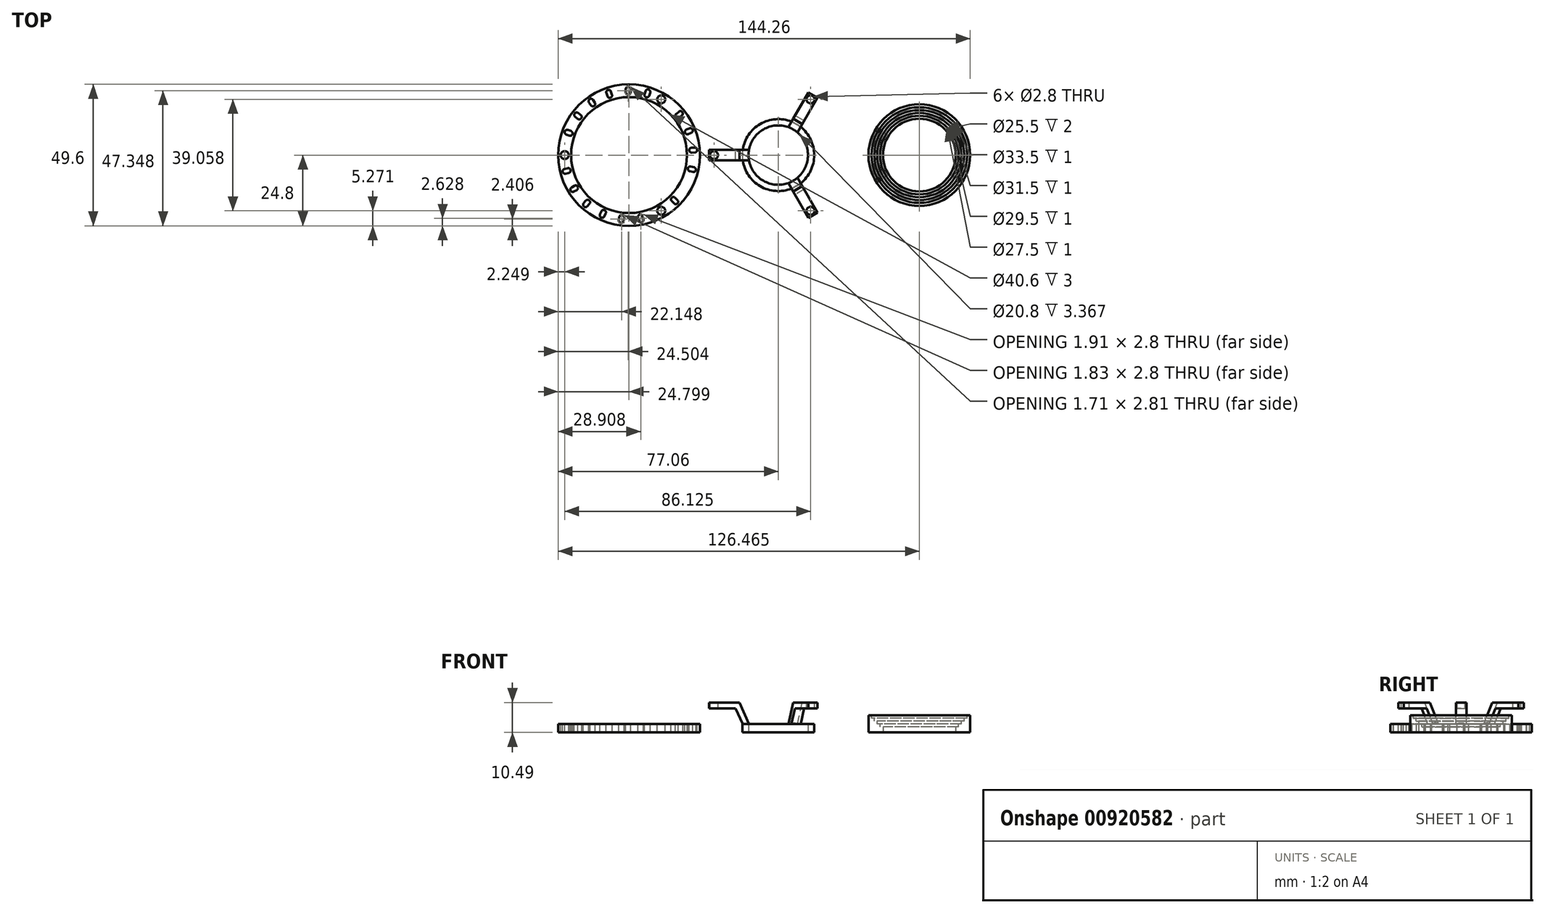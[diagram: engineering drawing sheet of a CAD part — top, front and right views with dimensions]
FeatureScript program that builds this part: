
annotation { "Feature Type Name" : "Feature", "Feature Type Description" : "" }
export const myFeature = defineFeature(function(context is Context, id is Id, definition is map)
    precondition{}
    {
        {
            var Q0;
            Q0=qCreatedBy(makeId("Top.planeOp"),FACE);
            var sketch = newSketch(context, id + "F0", { "sketchPlane" : qUnion([Q0])});
            skCircle(sketch, "E0", {"center": v(-52.66, 0) * mm, "radius": 24.8 * mm});
            skCircle(sketch, "E1", {"center": v(-52.66, 0) * mm, "radius": 20.3 * mm});
            skCircle(sketch, "E2.0", {"center": v(49, 0) * mm, "radius": 17.8 * mm});
            skCircle(sketch, "E3.0", {"center": v(49, 0) * mm, "radius": 12.75 * mm});
            skCircle(sketch, "E4.0", {"center": v(0, 0) * mm, "radius": 12.6 * mm});
            skCircle(sketch, "E5.0", {"center": v(0, 0) * mm, "radius": 10.4 * mm});
            skSolve(sketch);
        }
        {
            var Q0;
            Q0=makeQuery(id+"F0.imprint","IMPRINT",FACE,{"disambiguationData":[TD([[makeQuery(id+"F0.imprint","IMPRINT",EDGE,{"derivedFrom":sQuery(id+"F0.wireOp",EDGE,"E0")}),1.0]])]});
            var Q1;
            Q1=makeQuery(id+"F0.imprint","IMPRINT",FACE,{"disambiguationData":[TD([[makeQuery(id+"F0.imprint","IMPRINT",EDGE,{"derivedFrom":sQuery(id+"F0.wireOp",EDGE,"E4.0")}),1.0]])]});
            extrude(context, id + "F1", {"entities" : qUnion([Q0, Q1]), "depth" : 3 * mm, "offsetDistance" : 25 * mm});
        }
        {
            var Q0;
            Q0=makeQuery(id+"F1.opExtrude","CAP_FACE",FACE,{"disambiguationData":[OSD([sQuery(id+"F0.wireOp",EDGE,"E0"),sQuery(id+"F0.wireOp",EDGE,"E1")])],"isStart":false});
            var sketch = newSketch(context, id + "F2", { "sketchPlane" : qUnion([Q0])});
            skLineSegment(sketch, "E6", {"start": v(-72.96, 0) * mm, "end": v(-77.46, 0) * mm, "construction": true});
            skLineSegment(sketch, "E7.bottom", {"start": v(-72.88, 1.83) * mm, "end": v(-77.54, 1.83) * mm, "construction": true});
            skLineSegment(sketch, "E7.top", {"start": v(-72.88, -1.83) * mm, "end": v(-77.54, -1.83) * mm, "construction": true});
            skLineSegment(sketch, "E7.left", {"start": v(-72.88, 1.83) * mm, "end": v(-72.88, -1.83) * mm, "construction": true});
            skLineSegment(sketch, "E7.right", {"start": v(-77.54, 1.83) * mm, "end": v(-77.54, -1.83) * mm, "construction": true});
            skPoint(sketch, "E7.middle", {"position": v(-75.21, 0) * mm});
            skCircle(sketch, "E8", {"center": v(-75.21, 0) * mm, "radius": 1.4 * mm});
            skLineSegment(sketch, "E9.1.0", {"start": v(-40.72, 17.03) * mm, "end": v(-38.89, 20.2) * mm, "construction": true});
            skLineSegment(sketch, "E9.1.1", {"start": v(-43.89, 18.86) * mm, "end": v(-42.06, 22.03) * mm, "construction": true});
            skCircle(sketch, "E9.1.2", {"center": v(-41.39, 19.53) * mm, "radius": 1.4 * mm});
            skPoint(sketch, "E9.1.3", {"position": v(-41.39, 19.53) * mm});
            skLineSegment(sketch, "E9.1.4", {"start": v(-42.26, 18.01) * mm, "end": v(-40.51, 21.04) * mm, "construction": true});
            skLineSegment(sketch, "E9.1.5", {"start": v(-38.89, 20.2) * mm, "end": v(-42.06, 22.03) * mm, "construction": true});
            skLineSegment(sketch, "E9.1.6", {"start": v(-40.72, 17.03) * mm, "end": v(-43.89, 18.86) * mm, "construction": true});
            skLineSegment(sketch, "E9.2.0", {"start": v(-43.89, -18.86) * mm, "end": v(-42.06, -22.03) * mm, "construction": true});
            skLineSegment(sketch, "E9.2.1", {"start": v(-40.72, -17.03) * mm, "end": v(-38.89, -20.2) * mm, "construction": true});
            skCircle(sketch, "E9.2.2", {"center": v(-41.39, -19.53) * mm, "radius": 1.4 * mm});
            skPoint(sketch, "E9.2.3", {"position": v(-41.39, -19.53) * mm});
            skLineSegment(sketch, "E9.2.4", {"start": v(-42.26, -18.01) * mm, "end": v(-40.51, -21.04) * mm, "construction": true});
            skLineSegment(sketch, "E9.2.5", {"start": v(-42.06, -22.03) * mm, "end": v(-38.89, -20.2) * mm, "construction": true});
            skLineSegment(sketch, "E9.2.6", {"start": v(-43.89, -18.86) * mm, "end": v(-40.72, -17.03) * mm, "construction": true});
            skPoint(sketch, "E9.center", {"position": v(-52.66, 0) * mm});
            skLineSegment(sketch, "E10", {"start": v(-32.36, 0) * mm, "end": v(-27.86, 0) * mm, "construction": true});
            skLineSegment(sketch, "E11.left", {"start": v(-28.7, 0.05) * mm, "end": v(-28.7, -0.05) * mm});
            skLineSegment(sketch, "E11.right", {"start": v(-31.51, 0.05) * mm, "end": v(-31.51, -0.05) * mm});
            skPoint(sketch, "E11.middle", {"position": v(-30.11, 0) * mm});
            skPoint(sketch, "E12.visualSharp", {"position": v(-28.7, 0.85) * mm});
            skPoint(sketch, "E13.visualSharp", {"position": v(-31.51, 0.85) * mm});
            skPoint(sketch, "E14.visualSharp", {"position": v(-31.51, -0.85) * mm});
            skPoint(sketch, "E15.visualSharp", {"position": v(-28.7, -0.85) * mm});
            skPoint(sketch, "E16.1.0", {"position": v(-29.74, -7.02) * mm});
            skPoint(sketch, "E16.1.1", {"position": v(-32.45, -6.3) * mm});
            skPoint(sketch, "E16.1.2", {"position": v(-32.01, -4.66) * mm});
            skPoint(sketch, "E16.1.3", {"position": v(-29.3, -5.38) * mm});
            skPoint(sketch, "E16.1.4", {"position": v(-30.88, -5.84) * mm});
            skLineSegment(sketch, "E16.1.11", {"start": v(-32.57, -5.38) * mm, "end": v(-29.19, -6.29) * mm, "construction": true});
            skLineSegment(sketch, "E16.1.12", {"start": v(-32.22, -5.43) * mm, "end": v(-32.25, -5.52) * mm});
            skLineSegment(sketch, "E16.1.13", {"start": v(-29.51, -6.16) * mm, "end": v(-29.54, -6.24) * mm});
            skPoint(sketch, "E16.2.0", {"position": v(-32.34, -12.7) * mm});
            skPoint(sketch, "E16.2.1", {"position": v(-34.77, -11.3) * mm});
            skPoint(sketch, "E16.2.2", {"position": v(-33.92, -9.84) * mm});
            skPoint(sketch, "E16.2.3", {"position": v(-31.5, -11.24) * mm});
            skPoint(sketch, "E16.2.4", {"position": v(-33.13, -11.27) * mm});
            skLineSegment(sketch, "E16.2.11", {"start": v(-34.65, -10.4) * mm, "end": v(-31.62, -12.15) * mm, "construction": true});
            skLineSegment(sketch, "E16.2.12", {"start": v(-34.32, -10.53) * mm, "end": v(-34.37, -10.61) * mm});
            skLineSegment(sketch, "E16.2.13", {"start": v(-31.9, -11.94) * mm, "end": v(-31.94, -12.02) * mm});
            skPoint(sketch, "E16.3.0", {"position": v(-36.32, -17.53) * mm});
            skPoint(sketch, "E16.3.1", {"position": v(-38.3, -15.55) * mm});
            skPoint(sketch, "E16.3.2", {"position": v(-37.1, -14.36) * mm});
            skPoint(sketch, "E16.3.3", {"position": v(-35.13, -16.34) * mm});
            skPoint(sketch, "E16.3.4", {"position": v(-36.72, -15.95) * mm});
            skArc(sketch, "E16.3.5", {"start": v(-37.74, -14.99) * mm, "mid": v(-37.97, -15.55) * mm, "end": v(-37.74, -16.12) * mm});
            skArc(sketch, "E16.3.6", {"start": v(-36.89, -16.97) * mm, "mid": v(-36.32, -17.2) * mm, "end": v(-35.76, -16.97) * mm});
            skArc(sketch, "E16.3.7", {"start": v(-36.54, -14.92) * mm, "mid": v(-37.1, -14.69) * mm, "end": v(-37.68, -14.92) * mm});
            skArc(sketch, "E16.3.8", {"start": v(-35.7, -16.9) * mm, "mid": v(-35.46, -16.34) * mm, "end": v(-35.7, -15.77) * mm});
            skLineSegment(sketch, "E16.3.9", {"start": v(-35.7, -15.77) * mm, "end": v(-36.54, -14.92) * mm});
            skLineSegment(sketch, "E16.3.10", {"start": v(-36.89, -16.97) * mm, "end": v(-37.74, -16.12) * mm});
            skLineSegment(sketch, "E16.3.11", {"start": v(-37.95, -14.7) * mm, "end": v(-35.48, -17.18) * mm, "construction": true});
            skLineSegment(sketch, "E16.3.12", {"start": v(-37.68, -14.92) * mm, "end": v(-37.74, -14.99) * mm});
            skLineSegment(sketch, "E16.3.13", {"start": v(-35.7, -16.9) * mm, "end": v(-35.76, -16.97) * mm});
            skLineSegment(sketch, "E17.1.0", {"start": v(-42.77, -18.7) * mm, "end": v(-42.85, -18.74) * mm});
            skLineSegment(sketch, "E17.1.1", {"start": v(-41.47, -21.18) * mm, "end": v(-41.55, -21.22) * mm});
            skPoint(sketch, "E17.1.2", {"position": v(-42.26, -21.6) * mm});
            skArc(sketch, "E17.1.3", {"start": v(-41.7, -19.03) * mm, "mid": v(-42.16, -18.64) * mm, "end": v(-42.77, -18.7) * mm});
            skArc(sketch, "E17.1.4", {"start": v(-42.63, -20.88) * mm, "mid": v(-42.16, -21.27) * mm, "end": v(-41.55, -21.22) * mm});
            skArc(sketch, "E17.1.5", {"start": v(-42.85, -18.74) * mm, "mid": v(-43.25, -19.2) * mm, "end": v(-43.2, -19.82) * mm});
            skLineSegment(sketch, "E17.1.6", {"start": v(-42.98, -18.4) * mm, "end": v(-41.35, -21.5) * mm, "construction": true});
            skPoint(sketch, "E17.1.7", {"position": v(-42.16, -19.96) * mm});
            skPoint(sketch, "E17.1.8", {"position": v(-42.07, -18.32) * mm});
            skLineSegment(sketch, "E17.1.9", {"start": v(-41.13, -20.1) * mm, "end": v(-41.7, -19.03) * mm});
            skLineSegment(sketch, "E17.1.10", {"start": v(-42.63, -20.88) * mm, "end": v(-43.2, -19.82) * mm});
            skPoint(sketch, "E17.1.11", {"position": v(-40.76, -20.8) * mm});
            skPoint(sketch, "E17.1.12", {"position": v(-43.56, -19.1) * mm});
            skArc(sketch, "E17.1.13", {"start": v(-41.47, -21.18) * mm, "mid": v(-41.08, -20.7) * mm, "end": v(-41.13, -20.1) * mm});
            skLineSegment(sketch, "E17.2.0", {"start": v(-48.76, -20.79) * mm, "end": v(-48.85, -20.8) * mm});
            skLineSegment(sketch, "E17.2.1", {"start": v(-48.25, -23.54) * mm, "end": v(-48.34, -23.56) * mm});
            skPoint(sketch, "E17.2.2", {"position": v(-49.13, -23.7) * mm});
            skArc(sketch, "E17.2.3", {"start": v(-47.83, -21.43) * mm, "mid": v(-48.16, -20.91) * mm, "end": v(-48.76, -20.79) * mm});
            skArc(sketch, "E17.2.4", {"start": v(-49.27, -22.92) * mm, "mid": v(-48.94, -23.43) * mm, "end": v(-48.34, -23.56) * mm});
            skArc(sketch, "E17.2.5", {"start": v(-48.85, -20.8) * mm, "mid": v(-49.37, -21.14) * mm, "end": v(-49.5, -21.73) * mm});
            skLineSegment(sketch, "E17.2.6", {"start": v(-48.87, -20.45) * mm, "end": v(-48.23, -23.9) * mm, "construction": true});
            skPoint(sketch, "E17.2.7", {"position": v(-48.55, -22.17) * mm});
            skPoint(sketch, "E17.2.8", {"position": v(-47.98, -20.64) * mm});
            skLineSegment(sketch, "E17.2.9", {"start": v(-47.61, -22.6) * mm, "end": v(-47.83, -21.43) * mm});
            skLineSegment(sketch, "E17.2.10", {"start": v(-49.27, -22.92) * mm, "end": v(-49.5, -21.73) * mm});
            skPoint(sketch, "E17.2.11", {"position": v(-47.46, -23.4) * mm});
            skPoint(sketch, "E17.2.12", {"position": v(-49.64, -20.95) * mm});
            skArc(sketch, "E17.2.13", {"start": v(-48.25, -23.54) * mm, "mid": v(-47.74, -23.2) * mm, "end": v(-47.61, -22.6) * mm});
            skLineSegment(sketch, "E17.3.0", {"start": v(-55.1, -21) * mm, "end": v(-55.2, -21) * mm});
            skLineSegment(sketch, "E17.3.1", {"start": v(-55.43, -23.8) * mm, "end": v(-55.52, -23.78) * mm});
            skPoint(sketch, "E17.3.2", {"position": v(-56.32, -23.69) * mm});
            skArc(sketch, "E17.3.3", {"start": v(-54.4, -21.9) * mm, "mid": v(-54.57, -21.3) * mm, "end": v(-55.1, -21) * mm});
            skArc(sketch, "E17.3.4", {"start": v(-56.22, -22.9) * mm, "mid": v(-56.06, -23.48) * mm, "end": v(-55.52, -23.78) * mm});
            skArc(sketch, "E17.3.5", {"start": v(-55.2, -21) * mm, "mid": v(-55.78, -21.16) * mm, "end": v(-56.08, -21.7) * mm});
            skLineSegment(sketch, "E17.3.6", {"start": v(-55.1, -20.66) * mm, "end": v(-55.52, -24.13) * mm, "construction": true});
            skPoint(sketch, "E17.3.7", {"position": v(-55.31, -22.4) * mm});
            skPoint(sketch, "E17.3.8", {"position": v(-54.3, -21.1) * mm});
            skLineSegment(sketch, "E17.3.9", {"start": v(-54.54, -23.1) * mm, "end": v(-54.4, -21.9) * mm});
            skLineSegment(sketch, "E17.3.10", {"start": v(-56.22, -22.9) * mm, "end": v(-56.08, -21.7) * mm});
            skPoint(sketch, "E17.3.11", {"position": v(-54.64, -23.89) * mm});
            skPoint(sketch, "E17.3.12", {"position": v(-55.99, -20.9) * mm});
            skArc(sketch, "E17.3.13", {"start": v(-55.43, -23.8) * mm, "mid": v(-54.84, -23.63) * mm, "end": v(-54.54, -23.1) * mm});
            skLineSegment(sketch, "E17.4.0", {"start": v(-61.22, -19.34) * mm, "end": v(-61.3, -19.3) * mm});
            skLineSegment(sketch, "E17.4.1", {"start": v(-62.36, -21.9) * mm, "end": v(-62.44, -21.86) * mm});
            skPoint(sketch, "E17.4.2", {"position": v(-63.18, -21.54) * mm});
            skArc(sketch, "E17.4.3", {"start": v(-60.82, -20.4) * mm, "mid": v(-60.8, -19.78) * mm, "end": v(-61.22, -19.34) * mm});
            skArc(sketch, "E17.4.4", {"start": v(-62.85, -20.8) * mm, "mid": v(-62.87, -21.42) * mm, "end": v(-62.44, -21.86) * mm});
            skArc(sketch, "E17.4.5", {"start": v(-61.3, -19.3) * mm, "mid": v(-61.92, -19.29) * mm, "end": v(-62.36, -19.7) * mm});
            skLineSegment(sketch, "E17.4.6", {"start": v(-61.12, -19) * mm, "end": v(-62.54, -22.2) * mm, "construction": true});
            skPoint(sketch, "E17.4.7", {"position": v(-61.83, -20.6) * mm});
            skPoint(sketch, "E17.4.8", {"position": v(-60.49, -19.66) * mm});
            skLineSegment(sketch, "E17.4.9", {"start": v(-61.3, -21.5) * mm, "end": v(-60.82, -20.4) * mm});
            skLineSegment(sketch, "E17.4.10", {"start": v(-62.85, -20.8) * mm, "end": v(-62.36, -19.7) * mm});
            skPoint(sketch, "E17.4.11", {"position": v(-61.63, -22.23) * mm});
            skPoint(sketch, "E17.4.12", {"position": v(-62.04, -18.98) * mm});
            skArc(sketch, "E17.4.13", {"start": v(-62.36, -21.9) * mm, "mid": v(-61.75, -21.92) * mm, "end": v(-61.3, -21.5) * mm});
            skLineSegment(sketch, "E17.5.0", {"start": v(-66.57, -15.93) * mm, "end": v(-66.64, -15.87) * mm});
            skLineSegment(sketch, "E17.5.1", {"start": v(-68.42, -18.04) * mm, "end": v(-68.49, -17.98) * mm});
            skPoint(sketch, "E17.5.2", {"position": v(-69.09, -17.45) * mm});
            skArc(sketch, "E17.5.3", {"start": v(-66.5, -17.06) * mm, "mid": v(-66.3, -16.48) * mm, "end": v(-66.57, -15.93) * mm});
            skArc(sketch, "E17.5.4", {"start": v(-68.56, -16.85) * mm, "mid": v(-68.76, -17.43) * mm, "end": v(-68.49, -17.98) * mm});
            skArc(sketch, "E17.5.5", {"start": v(-66.64, -15.87) * mm, "mid": v(-67.22, -15.67) * mm, "end": v(-67.77, -15.94) * mm});
            skLineSegment(sketch, "E17.5.6", {"start": v(-66.38, -15.64) * mm, "end": v(-68.68, -18.27) * mm, "construction": true});
            skPoint(sketch, "E17.5.7", {"position": v(-67.53, -16.95) * mm});
            skPoint(sketch, "E17.5.8", {"position": v(-65.97, -16.46) * mm});
            skLineSegment(sketch, "E17.5.9", {"start": v(-67.3, -17.96) * mm, "end": v(-66.5, -17.06) * mm});
            skLineSegment(sketch, "E17.5.10", {"start": v(-68.56, -16.85) * mm, "end": v(-67.77, -15.94) * mm});
            skPoint(sketch, "E17.5.11", {"position": v(-67.82, -18.57) * mm});
            skPoint(sketch, "E17.5.12", {"position": v(-67.24, -15.34) * mm});
            skArc(sketch, "E17.5.13", {"start": v(-68.42, -18.04) * mm, "mid": v(-67.84, -18.24) * mm, "end": v(-67.3, -17.96) * mm});
            skLineSegment(sketch, "E17.6.0", {"start": v(-70.67, -11.09) * mm, "end": v(-70.72, -11.01) * mm});
            skLineSegment(sketch, "E17.6.1", {"start": v(-73.06, -12.55) * mm, "end": v(-73.1, -12.48) * mm});
            skPoint(sketch, "E17.6.2", {"position": v(-73.53, -11.8) * mm});
            skArc(sketch, "E17.6.3", {"start": v(-70.93, -12.19) * mm, "mid": v(-70.57, -11.7) * mm, "end": v(-70.67, -11.09) * mm});
            skArc(sketch, "E17.6.4", {"start": v(-72.84, -11.38) * mm, "mid": v(-73.2, -11.87) * mm, "end": v(-73.1, -12.48) * mm});
            skArc(sketch, "E17.6.5", {"start": v(-70.72, -11.01) * mm, "mid": v(-71.21, -10.65) * mm, "end": v(-71.82, -10.75) * mm});
            skLineSegment(sketch, "E17.6.6", {"start": v(-70.4, -10.87) * mm, "end": v(-73.38, -12.7) * mm, "construction": true});
            skPoint(sketch, "E17.6.7", {"position": v(-71.89, -11.78) * mm});
            skPoint(sketch, "E17.6.8", {"position": v(-70.25, -11.77) * mm});
            skLineSegment(sketch, "E17.6.9", {"start": v(-71.96, -12.82) * mm, "end": v(-70.93, -12.19) * mm});
            skLineSegment(sketch, "E17.6.10", {"start": v(-72.84, -11.38) * mm, "end": v(-71.82, -10.75) * mm});
            skPoint(sketch, "E17.6.11", {"position": v(-72.64, -13.24) * mm});
            skPoint(sketch, "E17.6.12", {"position": v(-71.13, -10.33) * mm});
            skArc(sketch, "E17.6.13", {"start": v(-73.06, -12.55) * mm, "mid": v(-72.56, -12.91) * mm, "end": v(-71.96, -12.82) * mm});
            skLineSegment(sketch, "E17.7.0", {"start": v(-73.15, -5.25) * mm, "end": v(-73.17, -5.16) * mm});
            skLineSegment(sketch, "E17.7.1", {"start": v(-75.87, -5.94) * mm, "end": v(-75.89, -5.85) * mm});
            skPoint(sketch, "E17.7.2", {"position": v(-76.08, -5.08) * mm});
            skArc(sketch, "E17.7.3", {"start": v(-73.73, -6.22) * mm, "mid": v(-73.24, -5.86) * mm, "end": v(-73.15, -5.25) * mm});
            skArc(sketch, "E17.7.4", {"start": v(-75.3, -4.88) * mm, "mid": v(-75.8, -5.25) * mm, "end": v(-75.89, -5.85) * mm});
            skArc(sketch, "E17.7.5", {"start": v(-73.17, -5.16) * mm, "mid": v(-73.54, -4.67) * mm, "end": v(-74.14, -4.58) * mm});
            skLineSegment(sketch, "E17.7.6", {"start": v(-72.82, -5.12) * mm, "end": v(-76.21, -5.98) * mm, "construction": true});
            skPoint(sketch, "E17.7.7", {"position": v(-74.52, -5.55) * mm});
            skPoint(sketch, "E17.7.8", {"position": v(-72.95, -6.03) * mm});
            skLineSegment(sketch, "E17.7.9", {"start": v(-74.9, -6.52) * mm, "end": v(-73.73, -6.22) * mm});
            skLineSegment(sketch, "E17.7.10", {"start": v(-75.3, -4.88) * mm, "end": v(-74.14, -4.58) * mm});
            skPoint(sketch, "E17.7.11", {"position": v(-75.67, -6.72) * mm});
            skPoint(sketch, "E17.7.12", {"position": v(-73.37, -4.39) * mm});
            skArc(sketch, "E17.7.13", {"start": v(-75.87, -5.94) * mm, "mid": v(-75.5, -6.43) * mm, "end": v(-74.9, -6.52) * mm});
            skLineSegment(sketch, "E17.8.0", {"start": v(-73.78, 1.06) * mm, "end": v(-73.78, 1.15) * mm});
            skLineSegment(sketch, "E17.8.1", {"start": v(-76.58, 1.2) * mm, "end": v(-76.58, 1.3) * mm});
            skPoint(sketch, "E17.8.2", {"position": v(-76.54, 2.1) * mm});
            skArc(sketch, "E17.8.3", {"start": v(-74.62, 0.3) * mm, "mid": v(-74.05, 0.5) * mm, "end": v(-73.78, 1.06) * mm});
            skArc(sketch, "E17.8.4", {"start": v(-75.74, 2.06) * mm, "mid": v(-76.31, 1.85) * mm, "end": v(-76.58, 1.3) * mm});
            skArc(sketch, "E17.8.5", {"start": v(-73.78, 1.15) * mm, "mid": v(-73.98, 1.73) * mm, "end": v(-74.54, 2) * mm});
            skLineSegment(sketch, "E17.8.6", {"start": v(-73.43, 1.09) * mm, "end": v(-76.93, 1.27) * mm, "construction": true});
            skPoint(sketch, "E17.8.7", {"position": v(-75.18, 1.18) * mm});
            skPoint(sketch, "E17.8.8", {"position": v(-73.82, 0.26) * mm});
            skLineSegment(sketch, "E17.8.9", {"start": v(-75.83, 0.37) * mm, "end": v(-74.62, 0.3) * mm});
            skLineSegment(sketch, "E17.8.10", {"start": v(-75.74, 2.06) * mm, "end": v(-74.54, 2) * mm});
            skPoint(sketch, "E17.8.11", {"position": v(-76.62, 0.4) * mm});
            skPoint(sketch, "E17.8.12", {"position": v(-73.74, 1.95) * mm});
            skArc(sketch, "E17.8.13", {"start": v(-76.58, 1.2) * mm, "mid": v(-76.38, 0.63) * mm, "end": v(-75.83, 0.37) * mm});
            skLineSegment(sketch, "E17.9.0", {"start": v(-72.52, 7.28) * mm, "end": v(-72.49, 7.36) * mm});
            skLineSegment(sketch, "E17.9.1", {"start": v(-75.15, 8.25) * mm, "end": v(-75.12, 8.33) * mm});
            skPoint(sketch, "E17.9.2", {"position": v(-74.84, 9.08) * mm});
            skArc(sketch, "E17.9.3", {"start": v(-73.55, 6.8) * mm, "mid": v(-72.93, 6.83) * mm, "end": v(-72.52, 7.28) * mm});
            skArc(sketch, "E17.9.4", {"start": v(-74.09, 8.8) * mm, "mid": v(-74.7, 8.78) * mm, "end": v(-75.12, 8.33) * mm});
            skArc(sketch, "E17.9.5", {"start": v(-72.49, 7.36) * mm, "mid": v(-72.51, 7.97) * mm, "end": v(-72.96, 8.4) * mm});
            skLineSegment(sketch, "E17.9.6", {"start": v(-72.18, 7.2) * mm, "end": v(-75.46, 8.41) * mm, "construction": true});
            skPoint(sketch, "E17.9.7", {"position": v(-73.82, 7.8) * mm});
            skPoint(sketch, "E17.9.8", {"position": v(-72.8, 6.53) * mm});
            skLineSegment(sketch, "E17.9.9", {"start": v(-74.67, 7.22) * mm, "end": v(-73.55, 6.8) * mm});
            skLineSegment(sketch, "E17.9.10", {"start": v(-74.09, 8.8) * mm, "end": v(-72.96, 8.4) * mm});
            skPoint(sketch, "E17.9.11", {"position": v(-75.43, 7.5) * mm});
            skPoint(sketch, "E17.9.12", {"position": v(-72.2, 8.11) * mm});
            skArc(sketch, "E17.9.13", {"start": v(-75.15, 8.25) * mm, "mid": v(-75.12, 7.64) * mm, "end": v(-74.67, 7.22) * mm});
            skLineSegment(sketch, "E17.10.0", {"start": v(-69.47, 12.84) * mm, "end": v(-69.41, 12.91) * mm});
            skLineSegment(sketch, "E17.10.1", {"start": v(-71.7, 14.55) * mm, "end": v(-71.64, 14.62) * mm});
            skPoint(sketch, "E17.10.2", {"position": v(-71.15, 15.25) * mm});
            skArc(sketch, "E17.10.3", {"start": v(-70.59, 12.7) * mm, "mid": v(-70, 12.53) * mm, "end": v(-69.47, 12.84) * mm});
            skArc(sketch, "E17.10.4", {"start": v(-70.51, 14.76) * mm, "mid": v(-71.1, 14.92) * mm, "end": v(-71.64, 14.62) * mm});
            skArc(sketch, "E17.10.5", {"start": v(-69.41, 12.91) * mm, "mid": v(-69.25, 13.5) * mm, "end": v(-69.56, 14.03) * mm});
            skLineSegment(sketch, "E17.10.6", {"start": v(-69.16, 12.66) * mm, "end": v(-71.94, 14.8) * mm, "construction": true});
            skPoint(sketch, "E17.10.7", {"position": v(-70.55, 13.73) * mm});
            skPoint(sketch, "E17.10.8", {"position": v(-69.95, 12.2) * mm});
            skLineSegment(sketch, "E17.10.9", {"start": v(-71.54, 13.42) * mm, "end": v(-70.59, 12.7) * mm});
            skLineSegment(sketch, "E17.10.10", {"start": v(-70.51, 14.76) * mm, "end": v(-69.56, 14.03) * mm});
            skPoint(sketch, "E17.10.11", {"position": v(-72.18, 13.91) * mm});
            skPoint(sketch, "E17.10.12", {"position": v(-68.92, 13.55) * mm});
            skArc(sketch, "E17.10.13", {"start": v(-71.7, 14.55) * mm, "mid": v(-71.85, 13.95) * mm, "end": v(-71.54, 13.42) * mm});
            skLineSegment(sketch, "E17.11.0", {"start": v(-64.9, 17.24) * mm, "end": v(-64.83, 17.3) * mm});
            skLineSegment(sketch, "E17.11.1", {"start": v(-66.52, 19.53) * mm, "end": v(-66.45, 19.59) * mm});
            skPoint(sketch, "E17.11.2", {"position": v(-65.8, 20.05) * mm});
            skArc(sketch, "E17.11.3", {"start": v(-66.02, 17.44) * mm, "mid": v(-65.5, 17.1) * mm, "end": v(-64.9, 17.24) * mm});
            skArc(sketch, "E17.11.4", {"start": v(-65.33, 19.4) * mm, "mid": v(-65.85, 19.72) * mm, "end": v(-66.45, 19.59) * mm});
            skArc(sketch, "E17.11.5", {"start": v(-64.83, 17.3) * mm, "mid": v(-64.5, 17.81) * mm, "end": v(-64.64, 18.41) * mm});
            skLineSegment(sketch, "E17.11.6", {"start": v(-64.67, 16.99) * mm, "end": v(-66.69, 19.84) * mm, "construction": true});
            skPoint(sketch, "E17.11.7", {"position": v(-65.68, 18.42) * mm});
            skPoint(sketch, "E17.11.8", {"position": v(-65.56, 16.78) * mm});
            skLineSegment(sketch, "E17.11.9", {"start": v(-66.71, 18.42) * mm, "end": v(-66.02, 17.44) * mm});
            skLineSegment(sketch, "E17.11.10", {"start": v(-65.33, 19.4) * mm, "end": v(-64.64, 18.41) * mm});
            skPoint(sketch, "E17.11.11", {"position": v(-67.18, 19.07) * mm});
            skPoint(sketch, "E17.11.12", {"position": v(-64.18, 17.76) * mm});
            skArc(sketch, "E17.11.13", {"start": v(-66.52, 19.53) * mm, "mid": v(-66.85, 19.02) * mm, "end": v(-66.71, 18.42) * mm});
            skLineSegment(sketch, "E17.12.0", {"start": v(-59.24, 20.1) * mm, "end": v(-59.15, 20.13) * mm});
            skLineSegment(sketch, "E17.12.1", {"start": v(-60.1, 22.77) * mm, "end": v(-60.02, 22.8) * mm});
            skPoint(sketch, "E17.12.2", {"position": v(-59.26, 23.04) * mm});
            skArc(sketch, "E17.12.3", {"start": v(-60.25, 20.61) * mm, "mid": v(-59.85, 20.15) * mm, "end": v(-59.24, 20.1) * mm});
            skArc(sketch, "E17.12.4", {"start": v(-59.01, 22.28) * mm, "mid": v(-59.4, 22.75) * mm, "end": v(-60.02, 22.8) * mm});
            skArc(sketch, "E17.12.5", {"start": v(-59.15, 20.13) * mm, "mid": v(-58.69, 20.52) * mm, "end": v(-58.64, 21.14) * mm});
            skLineSegment(sketch, "E17.12.6", {"start": v(-59.09, 19.78) * mm, "end": v(-60.17, 23.11) * mm, "construction": true});
            skPoint(sketch, "E17.12.7", {"position": v(-59.63, 21.45) * mm});
            skPoint(sketch, "E17.12.8", {"position": v(-60, 19.85) * mm});
            skLineSegment(sketch, "E17.12.9", {"start": v(-60.62, 21.76) * mm, "end": v(-60.25, 20.61) * mm});
            skLineSegment(sketch, "E17.12.10", {"start": v(-59.01, 22.28) * mm, "end": v(-58.64, 21.14) * mm});
            skPoint(sketch, "E17.12.11", {"position": v(-60.87, 22.52) * mm});
            skPoint(sketch, "E17.12.12", {"position": v(-58.4, 20.37) * mm});
            skArc(sketch, "E17.12.13", {"start": v(-60.1, 22.77) * mm, "mid": v(-60.57, 22.37) * mm, "end": v(-60.62, 21.76) * mm});
            skLineSegment(sketch, "E17.13.0", {"start": v(-52.98, 21.15) * mm, "end": v(-52.9, 21.15) * mm});
            skLineSegment(sketch, "E17.13.1", {"start": v(-53.02, 23.95) * mm, "end": v(-52.93, 23.95) * mm});
            skPoint(sketch, "E17.13.2", {"position": v(-52.13, 23.96) * mm});
            skArc(sketch, "E17.13.3", {"start": v(-53.8, 21.94) * mm, "mid": v(-53.55, 21.37) * mm, "end": v(-52.98, 21.15) * mm});
            skArc(sketch, "E17.13.4", {"start": v(-52.12, 23.16) * mm, "mid": v(-52.36, 23.72) * mm, "end": v(-52.93, 23.95) * mm});
            skArc(sketch, "E17.13.5", {"start": v(-52.9, 21.15) * mm, "mid": v(-52.33, 21.39) * mm, "end": v(-52.1, 21.96) * mm});
            skLineSegment(sketch, "E17.13.6", {"start": v(-52.93, 20.8) * mm, "end": v(-52.98, 24.3) * mm, "construction": true});
            skPoint(sketch, "E17.13.7", {"position": v(-52.96, 22.55) * mm});
            skPoint(sketch, "E17.13.8", {"position": v(-53.78, 21.14) * mm});
            skLineSegment(sketch, "E17.13.9", {"start": v(-53.81, 23.14) * mm, "end": v(-53.8, 21.94) * mm});
            skLineSegment(sketch, "E17.13.10", {"start": v(-52.12, 23.16) * mm, "end": v(-52.1, 21.96) * mm});
            skPoint(sketch, "E17.13.11", {"position": v(-53.82, 23.94) * mm});
            skPoint(sketch, "E17.13.12", {"position": v(-52.1, 21.16) * mm});
            skArc(sketch, "E17.13.13", {"start": v(-53.02, 23.95) * mm, "mid": v(-53.58, 23.7) * mm, "end": v(-53.81, 23.14) * mm});
            skLineSegment(sketch, "E17.14.0", {"start": v(-46.7, 20.29) * mm, "end": v(-46.61, 20.26) * mm});
            skLineSegment(sketch, "E17.14.1", {"start": v(-45.9, 22.98) * mm, "end": v(-45.81, 22.95) * mm});
            skPoint(sketch, "E17.14.2", {"position": v(-45.05, 22.73) * mm});
            skArc(sketch, "E17.14.3", {"start": v(-47.24, 21.28) * mm, "mid": v(-47.17, 20.68) * mm, "end": v(-46.7, 20.29) * mm});
            skArc(sketch, "E17.14.4", {"start": v(-45.27, 21.96) * mm, "mid": v(-45.34, 22.57) * mm, "end": v(-45.81, 22.95) * mm});
            skArc(sketch, "E17.14.5", {"start": v(-46.61, 20.26) * mm, "mid": v(-46, 20.33) * mm, "end": v(-45.62, 20.8) * mm});
            skLineSegment(sketch, "E17.14.6", {"start": v(-46.75, 19.94) * mm, "end": v(-45.76, 23.3) * mm, "construction": true});
            skPoint(sketch, "E17.14.7", {"position": v(-46.26, 21.62) * mm});
            skPoint(sketch, "E17.14.8", {"position": v(-47.47, 20.52) * mm});
            skLineSegment(sketch, "E17.14.9", {"start": v(-46.9, 22.44) * mm, "end": v(-47.24, 21.28) * mm});
            skLineSegment(sketch, "E17.14.10", {"start": v(-45.27, 21.96) * mm, "end": v(-45.62, 20.8) * mm});
            skPoint(sketch, "E17.14.11", {"position": v(-46.67, 23.2) * mm});
            skPoint(sketch, "E17.14.12", {"position": v(-45.84, 20.04) * mm});
            skArc(sketch, "E17.14.13", {"start": v(-45.9, 22.98) * mm, "mid": v(-46.51, 22.91) * mm, "end": v(-46.9, 22.44) * mm});
            skLineSegment(sketch, "E17.15.0", {"start": v(-40.95, 17.6) * mm, "end": v(-40.87, 17.56) * mm});
            skLineSegment(sketch, "E17.15.1", {"start": v(-39.4, 19.94) * mm, "end": v(-39.32, 19.9) * mm});
            skPoint(sketch, "E17.15.2", {"position": v(-38.65, 19.45) * mm});
            skArc(sketch, "E17.15.3", {"start": v(-41.17, 18.72) * mm, "mid": v(-41.3, 18.12) * mm, "end": v(-40.95, 17.6) * mm});
            skArc(sketch, "E17.15.4", {"start": v(-39.1, 18.78) * mm, "mid": v(-38.98, 19.38) * mm, "end": v(-39.32, 19.9) * mm});
            skArc(sketch, "E17.15.5", {"start": v(-40.87, 17.56) * mm, "mid": v(-40.27, 17.44) * mm, "end": v(-39.76, 17.78) * mm});
            skLineSegment(sketch, "E17.15.6", {"start": v(-41.1, 17.3) * mm, "end": v(-39.16, 20.2) * mm, "construction": true});
            skPoint(sketch, "E17.15.7", {"position": v(-40.13, 18.75) * mm});
            skPoint(sketch, "E17.15.8", {"position": v(-41.62, 18.05) * mm});
            skLineSegment(sketch, "E17.15.9", {"start": v(-40.5, 19.72) * mm, "end": v(-41.17, 18.72) * mm});
            skLineSegment(sketch, "E17.15.10", {"start": v(-39.1, 18.78) * mm, "end": v(-39.76, 17.78) * mm});
            skPoint(sketch, "E17.15.11", {"position": v(-40.06, 20.39) * mm});
            skPoint(sketch, "E17.15.12", {"position": v(-40.2, 17.11) * mm});
            skArc(sketch, "E17.15.13", {"start": v(-39.4, 19.94) * mm, "mid": v(-40, 20.06) * mm, "end": v(-40.5, 19.72) * mm});
            skLineSegment(sketch, "E17.16.0", {"start": v(-36.25, 13.34) * mm, "end": v(-36.2, 13.27) * mm});
            skLineSegment(sketch, "E17.16.1", {"start": v(-34.08, 15.1) * mm, "end": v(-34.02, 15.04) * mm});
            skPoint(sketch, "E17.16.2", {"position": v(-33.51, 14.42) * mm});
            skArc(sketch, "E17.16.3", {"start": v(-36.14, 14.47) * mm, "mid": v(-36.43, 13.93) * mm, "end": v(-36.25, 13.34) * mm});
            skArc(sketch, "E17.16.4", {"start": v(-34.14, 13.91) * mm, "mid": v(-33.84, 14.45) * mm, "end": v(-34.02, 15.04) * mm});
            skArc(sketch, "E17.16.5", {"start": v(-36.2, 13.27) * mm, "mid": v(-35.66, 12.98) * mm, "end": v(-35.07, 13.16) * mm});
            skLineSegment(sketch, "E17.16.6", {"start": v(-36.5, 13.09) * mm, "end": v(-33.78, 15.3) * mm, "construction": true});
            skPoint(sketch, "E17.16.7", {"position": v(-35.14, 14.2) * mm});
            skPoint(sketch, "E17.16.8", {"position": v(-36.76, 13.97) * mm});
            skLineSegment(sketch, "E17.16.9", {"start": v(-35.2, 15.23) * mm, "end": v(-36.14, 14.47) * mm});
            skLineSegment(sketch, "E17.16.10", {"start": v(-34.14, 13.91) * mm, "end": v(-35.07, 13.16) * mm});
            skPoint(sketch, "E17.16.11", {"position": v(-34.58, 15.73) * mm});
            skPoint(sketch, "E17.16.12", {"position": v(-35.7, 12.65) * mm});
            skArc(sketch, "E17.16.13", {"start": v(-34.08, 15.1) * mm, "mid": v(-34.61, 15.4) * mm, "end": v(-35.2, 15.23) * mm});
            skLineSegment(sketch, "E17.17.0", {"start": v(-33.04, 7.88) * mm, "end": v(-33, 7.8) * mm});
            skLineSegment(sketch, "E17.17.1", {"start": v(-30.43, 8.92) * mm, "end": v(-30.4, 8.83) * mm});
            skPoint(sketch, "E17.17.2", {"position": v(-30.1, 8.09) * mm});
            skArc(sketch, "E17.17.3", {"start": v(-32.59, 8.92) * mm, "mid": v(-33.03, 8.5) * mm, "end": v(-33.04, 7.88) * mm});
            skArc(sketch, "E17.17.4", {"start": v(-30.84, 7.8) * mm, "mid": v(-30.4, 8.22) * mm, "end": v(-30.4, 8.83) * mm});
            skArc(sketch, "E17.17.5", {"start": v(-33, 7.8) * mm, "mid": v(-32.57, 7.36) * mm, "end": v(-31.96, 7.35) * mm});
            skLineSegment(sketch, "E17.17.6", {"start": v(-33.34, 7.7) * mm, "end": v(-30.1, 9) * mm, "construction": true});
            skPoint(sketch, "E17.17.7", {"position": v(-31.72, 8.36) * mm});
            skPoint(sketch, "E17.17.8", {"position": v(-33.33, 8.62) * mm});
            skLineSegment(sketch, "E17.17.9", {"start": v(-31.47, 9.36) * mm, "end": v(-32.59, 8.92) * mm});
            skLineSegment(sketch, "E17.17.10", {"start": v(-30.84, 7.8) * mm, "end": v(-31.96, 7.35) * mm});
            skPoint(sketch, "E17.17.11", {"position": v(-30.73, 9.66) * mm});
            skPoint(sketch, "E17.17.12", {"position": v(-32.7, 7.05) * mm});
            skArc(sketch, "E17.17.13", {"start": v(-30.43, 8.92) * mm, "mid": v(-30.86, 9.36) * mm, "end": v(-31.47, 9.36) * mm});
            skLineSegment(sketch, "E17.18.0", {"start": v(-31.58, 1.7) * mm, "end": v(-31.57, 1.61) * mm});
            skLineSegment(sketch, "E17.18.1", {"start": v(-28.79, 1.92) * mm, "end": v(-28.78, 1.83) * mm});
            skPoint(sketch, "E17.18.2", {"position": v(-28.72, 1.04) * mm});
            skArc(sketch, "E17.18.3", {"start": v(-30.85, 2.57) * mm, "mid": v(-31.4, 2.29) * mm, "end": v(-31.58, 1.7) * mm});
            skArc(sketch, "E17.18.4", {"start": v(-29.51, 0.97) * mm, "mid": v(-28.97, 1.25) * mm, "end": v(-28.78, 1.83) * mm});
            skArc(sketch, "E17.18.5", {"start": v(-31.57, 1.61) * mm, "mid": v(-31.3, 1.07) * mm, "end": v(-30.71, 0.88) * mm});
            skLineSegment(sketch, "E17.18.6", {"start": v(-31.93, 1.63) * mm, "end": v(-28.44, 1.9) * mm, "construction": true});
            skPoint(sketch, "E17.18.7", {"position": v(-30.18, 1.77) * mm});
            skPoint(sketch, "E17.18.8", {"position": v(-31.64, 2.5) * mm});
            skLineSegment(sketch, "E17.18.9", {"start": v(-29.65, 2.66) * mm, "end": v(-30.85, 2.57) * mm});
            skLineSegment(sketch, "E17.18.10", {"start": v(-29.51, 0.97) * mm, "end": v(-30.71, 0.88) * mm});
            skPoint(sketch, "E17.18.11", {"position": v(-28.85, 2.72) * mm});
            skPoint(sketch, "E17.18.12", {"position": v(-31.51, 0.82) * mm});
            skArc(sketch, "E17.18.13", {"start": v(-28.79, 1.92) * mm, "mid": v(-29.06, 2.47) * mm, "end": v(-29.65, 2.66) * mm});
            skLineSegment(sketch, "E17.19.0", {"start": v(-32.02, -4.62) * mm, "end": v(-32.04, -4.71) * mm});
            skLineSegment(sketch, "E17.19.1", {"start": v(-29.29, -5.24) * mm, "end": v(-29.3, -5.33) * mm});
            skPoint(sketch, "E17.19.2", {"position": v(-29.49, -6.11) * mm});
            skArc(sketch, "E17.19.3", {"start": v(-31.07, -4.02) * mm, "mid": v(-31.67, -4.12) * mm, "end": v(-32.02, -4.62) * mm});
            skArc(sketch, "E17.19.4", {"start": v(-30.27, -5.93) * mm, "mid": v(-29.66, -5.83) * mm, "end": v(-29.3, -5.33) * mm});
            skArc(sketch, "E17.19.5", {"start": v(-32.04, -4.71) * mm, "mid": v(-31.94, -5.32) * mm, "end": v(-31.44, -5.67) * mm});
            skLineSegment(sketch, "E17.19.6", {"start": v(-32.37, -4.6) * mm, "end": v(-28.96, -5.36) * mm, "construction": true});
            skPoint(sketch, "E17.19.7", {"position": v(-30.67, -4.98) * mm});
            skPoint(sketch, "E17.19.8", {"position": v(-31.85, -3.84) * mm});
            skLineSegment(sketch, "E17.19.9", {"start": v(-29.9, -4.28) * mm, "end": v(-31.07, -4.02) * mm});
            skLineSegment(sketch, "E17.19.10", {"start": v(-30.27, -5.93) * mm, "end": v(-31.44, -5.67) * mm});
            skPoint(sketch, "E17.19.11", {"position": v(-29.11, -4.46) * mm});
            skPoint(sketch, "E17.19.12", {"position": v(-32.22, -5.5) * mm});
            skArc(sketch, "E17.19.13", {"start": v(-29.29, -5.24) * mm, "mid": v(-29.4, -4.64) * mm, "end": v(-29.9, -4.28) * mm});
            skArc(sketch, "E17.20.3", {"start": v(-33.23, -10.24) * mm, "mid": v(-33.84, -10.16) * mm, "end": v(-34.32, -10.53) * mm});
            skArc(sketch, "E17.20.4", {"start": v(-33.03, -12.3) * mm, "mid": v(-32.43, -12.39) * mm, "end": v(-31.94, -12.02) * mm});
            skArc(sketch, "E17.20.5", {"start": v(-34.37, -10.61) * mm, "mid": v(-34.45, -11.22) * mm, "end": v(-34.08, -11.7) * mm});
            skPoint(sketch, "E17.20.7", {"position": v(-33.13, -11.28) * mm});
            skLineSegment(sketch, "E17.20.9", {"start": v(-32.19, -10.84) * mm, "end": v(-33.23, -10.24) * mm});
            skLineSegment(sketch, "E17.20.10", {"start": v(-33.03, -12.3) * mm, "end": v(-34.08, -11.7) * mm});
            skArc(sketch, "E17.20.13", {"start": v(-31.9, -11.94) * mm, "mid": v(-31.82, -11.33) * mm, "end": v(-32.19, -10.84) * mm});
            skSolve(sketch);
        }
        {
            var Q0;
            Q0=makeQuery(id+"F2.imprint","IMPRINT",FACE,{"disambiguationData":[TD([[makeQuery(id+"F2.imprint","IMPRINT",EDGE,{"derivedFrom":sQuery(id+"F2.wireOp",EDGE,"E17.9.0")}),1.0]])]});
            var Q1;
            Q1=makeQuery(id+"F2.imprint","IMPRINT",FACE,{"disambiguationData":[TD([[makeQuery(id+"F2.imprint","IMPRINT",EDGE,{"derivedFrom":sQuery(id+"F2.wireOp",EDGE,"E17.10.0")}),1.0]])]});
            var Q2;
            Q2=makeQuery(id+"F2.imprint","IMPRINT",FACE,{"disambiguationData":[TD([[makeQuery(id+"F2.imprint","IMPRINT",EDGE,{"derivedFrom":sQuery(id+"F2.wireOp",EDGE,"E17.11.0")}),1.0]])]});
            var Q3;
            Q3=makeQuery(id+"F2.imprint","IMPRINT",FACE,{"disambiguationData":[TD([[makeQuery(id+"F2.imprint","IMPRINT",EDGE,{"derivedFrom":sQuery(id+"F2.wireOp",EDGE,"E17.12.0")}),1.0]])]});
            var Q4;
            Q4=makeQuery(id+"F2.imprint","IMPRINT",FACE,{"disambiguationData":[TD([[makeQuery(id+"F2.imprint","IMPRINT",EDGE,{"derivedFrom":sQuery(id+"F2.wireOp",EDGE,"E17.13.0")}),1.0]])]});
            var Q5;
            Q5=makeQuery(id+"F2.imprint","IMPRINT",FACE,{"disambiguationData":[TD([[makeQuery(id+"F2.imprint","IMPRINT",EDGE,{"derivedFrom":sQuery(id+"F2.wireOp",EDGE,"E17.14.0")}),1.0]])]});
            var Q6;
            {var subQ5=sQuery(id+"F2.wireOp",EDGE,"E17.15.9");Q6=makeQuery(id+"F2.imprint","IMPRINT",FACE,{"disambiguationData":[TD([[makeQuery(id+"F2.imprint","IMPRINT",EDGE,{"derivedFrom":subQ5}),-1.0]])]});}
            var Q7;
            {var subQ5=sQuery(id+"F2.wireOp",EDGE,"E17.15.9");Q7=makeQuery(id+"F2.imprint","IMPRINT",FACE,{"disambiguationData":[TD([[makeQuery(id+"F2.imprint","IMPRINT",EDGE,{"derivedFrom":subQ5}),1.0]])]});}
            var Q8;
            Q8=makeQuery(id+"F2.imprint","IMPRINT",FACE,{"disambiguationData":[TD([[makeQuery(id+"F2.imprint","IMPRINT",EDGE,{"derivedFrom":sQuery(id+"F2.wireOp",EDGE,"E17.16.0")}),1.0]])]});
            var Q9;
            Q9=makeQuery(id+"F2.imprint","IMPRINT",FACE,{"disambiguationData":[TD([[makeQuery(id+"F2.imprint","IMPRINT",EDGE,{"derivedFrom":sQuery(id+"F2.wireOp",EDGE,"E17.17.0")}),1.0]])]});
            var Q10;
            {var subQ5=sQuery(id+"F2.wireOp",EDGE,"E17.8.9");Q10=makeQuery(id+"F2.imprint","IMPRINT",FACE,{"disambiguationData":[TD([[makeQuery(id+"F2.imprint","IMPRINT",EDGE,{"derivedFrom":subQ5}),-1.0]])]});}
            var Q11;
            {var subQ5=sQuery(id+"F2.wireOp",EDGE,"E17.8.9");Q11=makeQuery(id+"F2.imprint","IMPRINT",FACE,{"disambiguationData":[TD([[makeQuery(id+"F2.imprint","IMPRINT",EDGE,{"derivedFrom":subQ5}),1.0]])]});}
            var Q12;
            Q12=makeQuery(id+"F2.imprint","IMPRINT",FACE,{"disambiguationData":[TD([[makeQuery(id+"F2.imprint","IMPRINT",EDGE,{"derivedFrom":sQuery(id+"F2.wireOp",EDGE,"E17.7.0")}),1.0]])]});
            var Q13;
            Q13=makeQuery(id+"F2.imprint","IMPRINT",FACE,{"disambiguationData":[TD([[makeQuery(id+"F2.imprint","IMPRINT",EDGE,{"derivedFrom":sQuery(id+"F2.wireOp",EDGE,"E17.6.0")}),1.0]])]});
            var Q14;
            Q14=makeQuery(id+"F2.imprint","IMPRINT",FACE,{"disambiguationData":[TD([[makeQuery(id+"F2.imprint","IMPRINT",EDGE,{"derivedFrom":sQuery(id+"F2.wireOp",EDGE,"E17.5.0")}),1.0]])]});
            var Q15;
            Q15=makeQuery(id+"F2.imprint","IMPRINT",FACE,{"disambiguationData":[TD([[makeQuery(id+"F2.imprint","IMPRINT",EDGE,{"derivedFrom":sQuery(id+"F2.wireOp",EDGE,"E17.4.0")}),1.0]])]});
            var Q16;
            Q16=makeQuery(id+"F2.imprint","IMPRINT",FACE,{"disambiguationData":[TD([[makeQuery(id+"F2.imprint","IMPRINT",EDGE,{"derivedFrom":sQuery(id+"F2.wireOp",EDGE,"E17.3.0")}),1.0]])]});
            var Q17;
            Q17=makeQuery(id+"F2.imprint","IMPRINT",FACE,{"disambiguationData":[TD([[makeQuery(id+"F2.imprint","IMPRINT",EDGE,{"derivedFrom":sQuery(id+"F2.wireOp",EDGE,"E17.2.0")}),1.0]])]});
            var Q18;
            {var subQ5=sQuery(id+"F2.wireOp",EDGE,"E17.1.9");Q18=makeQuery(id+"F2.imprint","IMPRINT",FACE,{"disambiguationData":[TD([[makeQuery(id+"F2.imprint","IMPRINT",EDGE,{"derivedFrom":subQ5}),1.0]])]});}
            var Q19;
            {var subQ5=sQuery(id+"F2.wireOp",EDGE,"E17.1.9");Q19=makeQuery(id+"F2.imprint","IMPRINT",FACE,{"disambiguationData":[TD([[makeQuery(id+"F2.imprint","IMPRINT",EDGE,{"derivedFrom":subQ5}),-1.0]])]});}
            var Q20;
            Q20=makeQuery(id+"F2.imprint","IMPRINT",FACE,{"disambiguationData":[TD([[makeQuery(id+"F2.imprint","IMPRINT",EDGE,{"derivedFrom":sQuery(id+"F2.wireOp",EDGE,"E16.3.5")}),1.0]])]});
            var Q21;
            Q21=makeQuery(id+"F2.imprint","IMPRINT",FACE,{"disambiguationData":[TD([[makeQuery(id+"F2.imprint","IMPRINT",EDGE,{"derivedFrom":sQuery(id+"F2.wireOp",EDGE,"E16.2.12")}),1.0]])]});
            var Q22;
            Q22=makeQuery(id+"F2.imprint","IMPRINT",FACE,{"disambiguationData":[TD([[makeQuery(id+"F2.imprint","IMPRINT",EDGE,{"derivedFrom":sQuery(id+"F2.wireOp",EDGE,"E17.19.0")}),1.0]])]});
            var Q23;
            Q23=makeQuery(id+"F2.imprint","IMPRINT",FACE,{"disambiguationData":[TD([[makeQuery(id+"F2.imprint","IMPRINT",EDGE,{"derivedFrom":sQuery(id+"F2.wireOp",EDGE,"E17.18.0")}),1.0]])]});
            extrude(context, id + "F3", {"entities" : qUnion([Q0, Q1, Q2, Q3, Q4, Q5, Q6, Q7, Q8, Q9, Q10, Q11, Q12, Q13, Q14, Q15, Q16, Q17, Q18, Q19, Q20, Q21, Q22, Q23]), "operationType" : NewBodyOperationType.REMOVE, "oppositeDirection" : true, "depth" : 3 * mm, "offsetDistance" : 25 * mm});
        }
        {
            var Q0;
            Q0=makeQuery(id+"F1.opExtrude","CAP_FACE",FACE,{"disambiguationData":[OSD([sQuery(id+"F0.wireOp",EDGE,"E4.0"),sQuery(id+"F0.wireOp",EDGE,"E5.0")])],"isStart":false});
            var sketch = newSketch(context, id + "F4", { "sketchPlane" : qUnion([Q0])});
            skLineSegment(sketch, "E18.bottom", {"start": v(-24.3, 1.85) * mm, "end": v(0, 1.85) * mm});
            skLineSegment(sketch, "E18.top", {"start": v(-24.3, -1.85) * mm, "end": v(0, -1.85) * mm});
            skLineSegment(sketch, "E18.left", {"start": v(-24.3, 1.85) * mm, "end": v(-24.3, -1.85) * mm});
            skPoint(sketch, "E18.middle", {"position": v(0, 0) * mm});
            skLineSegment(sketch, "E19", {"start": v(0, 1.85) * mm, "end": v(0, -1.85) * mm});
            skPoint(sketch, "E18.right.end.orphan", {"position": v(24.3, -1.85) * mm});
            skPoint(sketch, "E18.right.start.orphan", {"position": v(24.3, 1.85) * mm});
            skLineSegment(sketch, "E20.1.1", {"start": v(13.75, 20.12) * mm, "end": v(1.6, -0.93) * mm});
            skLineSegment(sketch, "E20.1.2", {"start": v(13.75, 20.12) * mm, "end": v(10.55, 21.97) * mm});
            skLineSegment(sketch, "E20.1.3", {"start": v(1.6, -0.93) * mm, "end": v(-1.6, 0.93) * mm});
            skLineSegment(sketch, "E20.1.4", {"start": v(10.55, 21.97) * mm, "end": v(-1.6, 0.93) * mm});
            skLineSegment(sketch, "E20.2.1", {"start": v(10.55, -21.97) * mm, "end": v(-1.6, -0.93) * mm});
            skLineSegment(sketch, "E20.2.2", {"start": v(10.55, -21.97) * mm, "end": v(13.75, -20.12) * mm});
            skLineSegment(sketch, "E20.2.3", {"start": v(-1.6, -0.93) * mm, "end": v(1.6, 0.93) * mm});
            skLineSegment(sketch, "E20.2.4", {"start": v(13.75, -20.12) * mm, "end": v(1.6, 0.93) * mm});
            skLineSegment(sketch, "E20.anchor1", {"start": v(0, 0) * mm, "end": v(-24.3, -1.85) * mm, "construction": true});
            skLineSegment(sketch, "E20.anchor2", {"start": v(0, 0) * mm, "end": v(13.75, -20.12) * mm, "construction": true});
            skSolve(sketch);
        }
        {
            var Q0;
            Q0=makeQuery(id+"F0.imprint","IMPRINT",FACE,{"disambiguationData":[TD([[makeQuery(id+"F0.imprint","IMPRINT",EDGE,{"derivedFrom":sQuery(id+"F0.wireOp",EDGE,"E2.0")}),1.0]])]});
            extrude(context, id + "F5", {"entities" : qUnion([Q0]), "depth" : 6 * mm, "offsetDistance" : 25 * mm});
        }
        {
            var Q0;
            Q0=makeQuery(id+"F5.opExtrude","CAP_FACE",FACE,{"disambiguationData":[OSD([sQuery(id+"F0.wireOp",EDGE,"E2.0"),sQuery(id+"F0.wireOp",EDGE,"E3.0")])],"isStart":false});
            var sketch = newSketch(context, id + "F6", { "sketchPlane" : qUnion([Q0])});
            skCircle(sketch, "E21.0", {"center": v(49, 0) * mm, "radius": 13.75 * mm});
            skCircle(sketch, "E22.0", {"center": v(49, 0) * mm, "radius": 14.75 * mm});
            skCircle(sketch, "E23.0", {"center": v(49, 0) * mm, "radius": 15.75 * mm});
            skCircle(sketch, "E24.0", {"center": v(49, 0) * mm, "radius": 16.75 * mm});
            skCircle(sketch, "E25.0", {"center": v(49, 0) * mm, "radius": 17.75 * mm});
            skSolve(sketch);
        }
        {
            var Q0;
            Q0=makeQuery(id+"F6.imprint","IMPRINT",FACE,{"disambiguationData":[TD([[makeQuery(id+"F6.imprint","IMPRINT",EDGE,{"derivedFrom":sQuery(id+"F6.wireOp",EDGE,"E23.0")}),-1.0]])]});
            extrude(context, id + "F7", {"entities" : qUnion([Q0]), "operationType" : NewBodyOperationType.REMOVE, "oppositeDirection" : true, "depth" : 1 * mm, "offsetDistance" : 25 * mm});
        }
        {
            var Q0;
            Q0=makeQuery(id+"F6.imprint","IMPRINT",FACE,{"disambiguationData":[TD([[makeQuery(id+"F6.imprint","IMPRINT",EDGE,{"derivedFrom":sQuery(id+"F6.wireOp",EDGE,"E22.0")}),-1.0]])]});
            extrude(context, id + "F8", {"entities" : qUnion([Q0]), "operationType" : NewBodyOperationType.REMOVE, "oppositeDirection" : true, "depth" : 2 * mm, "offsetDistance" : 25 * mm});
        }
        {
            var Q0;
            Q0=makeQuery(id+"F6.imprint","IMPRINT",FACE,{"disambiguationData":[TD([[makeQuery(id+"F6.imprint","IMPRINT",EDGE,{"derivedFrom":sQuery(id+"F6.wireOp",EDGE,"E21.0")}),-1.0]])]});
            extrude(context, id + "F9", {"entities" : qUnion([Q0]), "operationType" : NewBodyOperationType.REMOVE, "oppositeDirection" : true, "depth" : 3 * mm, "offsetDistance" : 25 * mm});
        }
        {
            var Q0;
            Q0=makeQuery(id+"F6.imprint","IMPRINT",FACE,{"disambiguationData":[TD([[makeQuery(id+"F6.imprint","IMPRINT",EDGE,{"derivedFrom":sQuery(id+"F6.wireOp",EDGE,"E21.0")}),1.0]])]});
            extrude(context, id + "F10", {"entities" : qUnion([Q0]), "operationType" : NewBodyOperationType.REMOVE, "oppositeDirection" : true, "depth" : 4 * mm, "offsetDistance" : 25 * mm});
        }
        {
            var Q0;
            {var subQ0=sQuery(id+"F4.wireOp",EDGE,"E20.2.2");Q0=makeQuery(id+"F4.imprint","IMPRINT",FACE,{"disambiguationData":[TD([[makeQuery(id+"F4.imprint","IMPRINT",EDGE,{"derivedFrom":subQ0}),1.0]])]});}
            var Q1;
            {var subQ0=sQuery(id+"F4.wireOp",EDGE,"E18.left");Q1=makeQuery(id+"F4.imprint","IMPRINT",FACE,{"disambiguationData":[TD([[makeQuery(id+"F4.imprint","IMPRINT",EDGE,{"derivedFrom":subQ0}),1.0]])]});}
            var Q2;
            {var subQ0=sQuery(id+"F4.wireOp",EDGE,"E18.bottom");var subQ1=makeQuery(id+"F1.opExtrude","CAP_EDGE",EDGE,{"disambiguationData":[OSD([sQuery(id+"F0.wireOp",EDGE,"E4.0")])],"isStart":false});var subQ2=makeQuery(id+"F4.imprint","INTERSECT",VERTEX,{"derivedFrom":[subQ1,subQ0]});Q2=makeQuery(id+"F4.imprint","IMPRINT",FACE,{"disambiguationData":[TD([[makeQuery(id+"F4.imprint","IMPRINT",EDGE,{"disambiguationData":[TD([[subQ2,-1.0]])],"derivedFrom":subQ0}),-1.0]])]});}
            var Q3;
            {var subQ0=sQuery(id+"F4.wireOp",EDGE,"E20.1.1");var subQ1=makeQuery(id+"F1.opExtrude","CAP_EDGE",EDGE,{"disambiguationData":[OSD([sQuery(id+"F0.wireOp",EDGE,"E4.0")])],"isStart":false});var subQ2=makeQuery(id+"F4.imprint","INTERSECT",VERTEX,{"derivedFrom":[subQ1,subQ0]});Q3=makeQuery(id+"F4.imprint","IMPRINT",FACE,{"disambiguationData":[TD([[makeQuery(id+"F4.imprint","IMPRINT",EDGE,{"disambiguationData":[TD([[subQ2,-1.0]])],"derivedFrom":subQ0}),-1.0]])]});}
            var Q4;
            {var subQ0=sQuery(id+"F4.wireOp",EDGE,"E20.1.2");Q4=makeQuery(id+"F4.imprint","IMPRINT",FACE,{"disambiguationData":[TD([[makeQuery(id+"F4.imprint","IMPRINT",EDGE,{"derivedFrom":subQ0}),1.0]])]});}
            var Q5;
            {var subQ0=sQuery(id+"F4.wireOp",EDGE,"E20.2.1");var subQ1=makeQuery(id+"F1.opExtrude","CAP_EDGE",EDGE,{"disambiguationData":[OSD([sQuery(id+"F0.wireOp",EDGE,"E4.0")])],"isStart":false});var subQ2=makeQuery(id+"F4.imprint","INTERSECT",VERTEX,{"derivedFrom":[subQ1,subQ0]});Q5=makeQuery(id+"F4.imprint","IMPRINT",FACE,{"disambiguationData":[TD([[makeQuery(id+"F4.imprint","IMPRINT",EDGE,{"disambiguationData":[TD([[subQ2,-1.0]])],"derivedFrom":subQ0}),-1.0]])]});}
            extrude(context, id + "F11", {"entities" : qUnion([Q0, Q1, Q2, Q3, Q4, Q5]), "operationType" : NewBodyOperationType.ADD, "depth" : 8 * mm, "offsetDistance" : 25 * mm});
        }
        {
            var Q0;
            Q0=makeQuery(id+"F11.opExtrude","SWEPT_FACE",FACE,{"disambiguationData":[OSD([sQuery(id+"F4.wireOp",EDGE,"E20.2.1")])]});
            var sketch = newSketch(context, id + "F12", { "sketchPlane" : qUnion([Q0])});
            skLineSegment(sketch, "E26", {"start": v(12.46, 3) * mm, "end": v(14.94, 8.46) * mm});
            skLineSegment(sketch, "E27", {"start": v(14.94, 8.46) * mm, "end": v(24.3, 8.46) * mm});
            skLineSegment(sketch, "E28", {"start": v(10.23, 3) * mm, "end": v(13.63, 10.5) * mm});
            skLineSegment(sketch, "E29", {"start": v(24.3, 10.5) * mm, "end": v(13.63, 10.5) * mm});
            skPoint(sketch, "E30.end.orphan", {"position": v(17.25, 10.5) * mm});
            skLineSegment(sketch, "E31", {"start": v(24.3, 8.46) * mm, "end": v(24.3, 10.5) * mm});
            skLineSegment(sketch, "E32", {"start": v(12.46, 3) * mm, "end": v(10.23, 3) * mm});
            skSolve(sketch);
        }
        {
            var Q0;
            Q0=makeQuery(id+"F11.opExtrude","SWEPT_FACE",FACE,{"disambiguationData":[OSD([sQuery(id+"F4.wireOp",EDGE,"E18.bottom")])]});
            var sketch = newSketch(context, id + "F13", { "sketchPlane" : qUnion([Q0])});
            skLineSegment(sketch, "E33", {"start": v(12.46, 3) * mm, "end": v(14.94, 8.46) * mm});
            skLineSegment(sketch, "E34", {"start": v(14.94, 8.46) * mm, "end": v(24.3, 8.46) * mm});
            skLineSegment(sketch, "E35", {"start": v(10.23, 3) * mm, "end": v(13.63, 10.5) * mm});
            skLineSegment(sketch, "E36", {"start": v(24.3, 10.5) * mm, "end": v(13.63, 10.5) * mm});
            skPoint(sketch, "E37.end.orphan", {"position": v(17.25, 10.5) * mm});
            skLineSegment(sketch, "E38", {"start": v(24.3, 8.46) * mm, "end": v(24.3, 10.5) * mm});
            skLineSegment(sketch, "E39", {"start": v(12.46, 3) * mm, "end": v(10.23, 3) * mm});
            skSolve(sketch);
        }
        {
            var Q0;
            Q0=makeQuery(id+"F11.opExtrude","SWEPT_FACE",FACE,{"disambiguationData":[OSD([sQuery(id+"F4.wireOp",EDGE,"E20.1.1")])]});
            var sketch = newSketch(context, id + "F14", { "sketchPlane" : qUnion([Q0])});
            skLineSegment(sketch, "E40", {"start": v(12.46, 3) * mm, "end": v(14.94, 8.46) * mm});
            skLineSegment(sketch, "E41", {"start": v(14.94, 8.46) * mm, "end": v(24.3, 8.46) * mm});
            skLineSegment(sketch, "E42", {"start": v(10.23, 3) * mm, "end": v(13.63, 10.5) * mm});
            skLineSegment(sketch, "E43", {"start": v(24.3, 10.5) * mm, "end": v(13.63, 10.5) * mm});
            skPoint(sketch, "E44.end.orphan", {"position": v(17.25, 10.5) * mm});
            skLineSegment(sketch, "E45", {"start": v(24.3, 8.46) * mm, "end": v(24.3, 10.5) * mm});
            skLineSegment(sketch, "E46", {"start": v(12.46, 3) * mm, "end": v(10.23, 3) * mm});
            skSolve(sketch);
        }
        {
            var Q0;
            Q0=makeQuery(id+"F14.imprint","IMPRINT",FACE,{"disambiguationData":[TD([[makeQuery(id+"F14.imprint","IMPRINT",EDGE,{"derivedFrom":sQuery(id+"F14.wireOp",EDGE,"E42")}),1.0]])]});
            var Q1;
            Q1=makeQuery(id+"F14.imprint","IMPRINT",FACE,{"disambiguationData":[TD([[makeQuery(id+"F14.imprint","IMPRINT",EDGE,{"derivedFrom":sQuery(id+"F14.wireOp",EDGE,"E40")}),-1.0]])]});
            extrude(context, id + "F15", {"entities" : qUnion([Q0, Q1]), "operationType" : NewBodyOperationType.REMOVE, "oppositeDirection" : true, "depth" : 25 * mm, "offsetDistance" : 25 * mm});
        }
        {
            var Q0;
            Q0=makeQuery(id+"F12.imprint","IMPRINT",FACE,{"disambiguationData":[TD([[makeQuery(id+"F12.imprint","IMPRINT",EDGE,{"derivedFrom":sQuery(id+"F12.wireOp",EDGE,"E26")}),-1.0]])]});
            var Q1;
            Q1=makeQuery(id+"F12.imprint","IMPRINT",FACE,{"disambiguationData":[TD([[makeQuery(id+"F12.imprint","IMPRINT",EDGE,{"derivedFrom":sQuery(id+"F12.wireOp",EDGE,"E28")}),1.0]])]});
            extrude(context, id + "F16", {"entities" : qUnion([Q0, Q1]), "operationType" : NewBodyOperationType.REMOVE, "oppositeDirection" : true, "depth" : 25 * mm, "offsetDistance" : 25 * mm});
        }
        {
            var Q0;
            Q0=makeQuery(id+"F13.imprint","IMPRINT",FACE,{"disambiguationData":[TD([[makeQuery(id+"F13.imprint","IMPRINT",EDGE,{"derivedFrom":sQuery(id+"F13.wireOp",EDGE,"E35")}),1.0]])]});
            var Q1;
            Q1=makeQuery(id+"F13.imprint","IMPRINT",FACE,{"disambiguationData":[TD([[makeQuery(id+"F13.imprint","IMPRINT",EDGE,{"derivedFrom":sQuery(id+"F13.wireOp",EDGE,"E33")}),-1.0]])]});
            extrude(context, id + "F17", {"entities" : qUnion([Q0, Q1]), "operationType" : NewBodyOperationType.REMOVE, "oppositeDirection" : true, "depth" : 25 * mm, "offsetDistance" : 25 * mm});
        }
        {
            var Q0;
            Q0=makeQuery(id+"F1.opExtrude","SWEPT_BODY",BODY,{"disambiguationData":[OSD([sQuery(id+"F0.wireOp",EDGE,"E4.0"),sQuery(id+"F0.wireOp",EDGE,"E5.0")])]});
            transform(context, id + "F18", {"entities" : qUnion([Q0]), "transformType" : TransformType.TRANSLATION_3D, "dx" : -52.7 * mm, "dy" : 0 * mm, "dz" : 0 * mm, "makeCopy" : false});
        }
        {
            var Q0;
            Q0=makeQuery(id+"F15.boolean.opBoolean","COPY",FACE,{"derivedFrom":makeQuery(id+"F15.opExtrude","SWEPT_FACE",FACE,{"disambiguationData":[OSD([sQuery(id+"F14.wireOp",EDGE,"E43")])]})});
            var sketch = newSketch(context, id + "F19", { "sketchPlane" : qUnion([Q0])});
            skCircle(sketch, "E47.0", {"center": v(-41.39, 19.53) * mm, "radius": 1.4 * mm});
            skCircle(sketch, "E48.0", {"center": v(-75.21, 0) * mm, "radius": 1.4 * mm});
            skCircle(sketch, "E49.0", {"center": v(-41.39, -19.53) * mm, "radius": 1.4 * mm});
            skSolve(sketch);
        }
        {
            var Q0;
            Q0=makeQuery(id+"F19.imprint","IMPRINT",FACE,{"disambiguationData":[TD([[makeQuery(id+"F19.imprint","IMPRINT",EDGE,{"derivedFrom":sQuery(id+"F19.wireOp",EDGE,"E48.0")}),1.0]])]});
            var Q1;
            Q1=makeQuery(id+"F19.imprint","IMPRINT",FACE,{"disambiguationData":[TD([[makeQuery(id+"F19.imprint","IMPRINT",EDGE,{"derivedFrom":sQuery(id+"F19.wireOp",EDGE,"E47.0")}),1.0]])]});
            var Q2;
            Q2=makeQuery(id+"F19.imprint","IMPRINT",FACE,{"disambiguationData":[TD([[makeQuery(id+"F19.imprint","IMPRINT",EDGE,{"derivedFrom":sQuery(id+"F19.wireOp",EDGE,"E49.0")}),1.0]])]});
            extrude(context, id + "F20", {"entities" : qUnion([Q0, Q1, Q2]), "operationType" : NewBodyOperationType.REMOVE, "oppositeDirection" : true, "depth" : 3 * mm, "offsetDistance" : 25 * mm});
        }
        {
            var Q0;
            Q0=makeQuery(id+"F1.opExtrude","SWEPT_BODY",BODY,{"disambiguationData":[OSD([sQuery(id+"F0.wireOp",EDGE,"E4.0"),sQuery(id+"F0.wireOp",EDGE,"E5.0")])]});
            transform(context, id + "F21", {"entities" : qUnion([Q0]), "transformType" : TransformType.TRANSLATION_3D, "dx" : 52.3 * mm, "dy" : 0 * mm, "dz" : 0 * mm, "makeCopy" : false});
        }
    });
